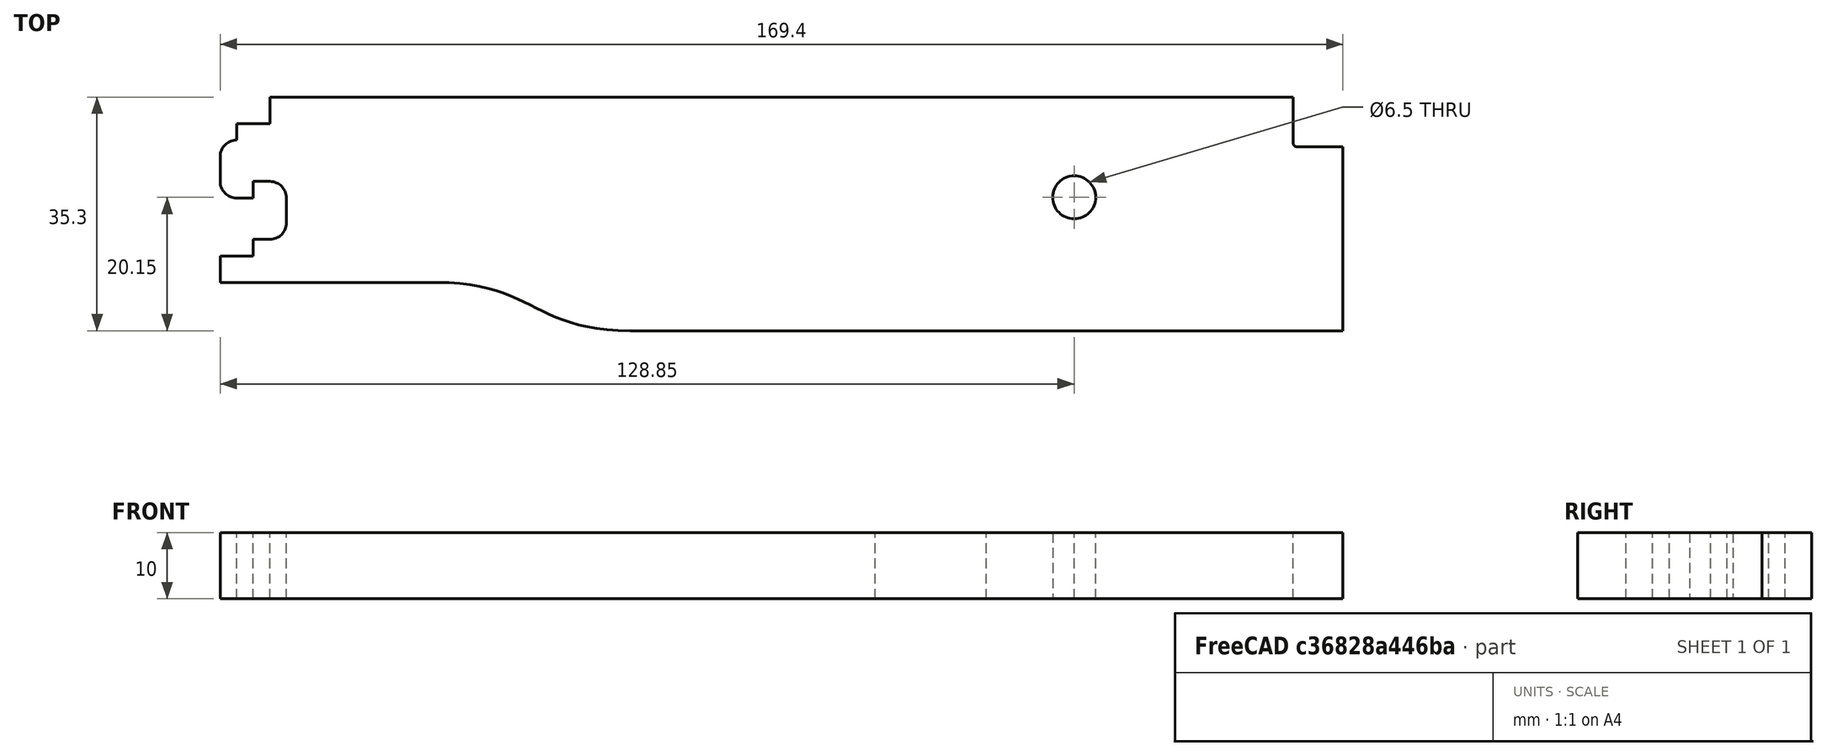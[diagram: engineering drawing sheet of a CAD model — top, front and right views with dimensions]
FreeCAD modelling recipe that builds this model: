
FCSTD DOCUMENT  (FreeCAD 0.19R0.19.2)
Label: v0_08
License: All rights reserved
LicenseURL: http://en.wikipedia.org/wiki/All_rights_reserved
objects: Sketcher::SketchObject×1, Part::Extrusion×1
note: 2 computed .brp shape members not serialized (recipe doc carries the construction recipe); baked Part::Feature solids carry a one-line shape summary decoded from their .brp

FEATURE [Sketcher::SketchObject] Sketch
  FullyConstrained = true
  sketch-geometry (43):
    g0: LineSegment StartX=0 StartY=0 StartZ=0 EndX=111.35 EndY=0 EndZ=0
    g1: Circle CenterX=111.35 CenterY=-15.15 CenterZ=0 NormalX=0 NormalY=0 NormalZ=1 AngleXU=0 Radius=3.25
    g2: LineSegment StartX=111.35 StartY=0 StartZ=0 EndX=144.4 EndY=0 EndZ=0
    g3: LineSegment StartX=144.9 StartY=-7.5 StartZ=0 EndX=151.9 EndY=-7.5 EndZ=0
    g4: LineSegment StartX=111.35 StartY=0 StartZ=0 EndX=98.1 EndY=0 EndZ=0
    g5: LineSegment StartX=111.35 StartY=0 StartZ=0 EndX=81.35 EndY=0 EndZ=0
    g6: LineSegment StartX=144.4 StartY=0 StartZ=0 EndX=144.4 EndY=-7 EndZ=0
    g7: ArcOfCircle CenterX=144.9 CenterY=-7 CenterZ=0 NormalX=0 NormalY=0 NormalZ=1 AngleXU=0 Radius=0.5 StartAngle=3.14159 EndAngle=4.71239
    g8: LineSegment StartX=151.9 StartY=-7.5 StartZ=0 EndX=151.9 EndY=-20.4 EndZ=0
    g9: LineSegment StartX=44.35 StartY=-35.3 StartZ=0 EndX=81.35 EndY=-35.3 EndZ=0
    g10: LineSegment StartX=81.35 StartY=-35.3 StartZ=0 EndX=151.9 EndY=-35.3 EndZ=0
    g11: LineSegment StartX=151.9 StartY=-20.4 StartZ=0 EndX=151.9 EndY=-35.3 EndZ=0
    g12-g16: Circle x5 (B-spline internal-alignment scaffolding for g17; pole/knot coordinates omitted)
    g17: BSplineCurve PolesCount=5 KnotsCount=3 Degree=3 IsPeriodic=0
    g18: GeomPoint X=15.15 Y=-28 Z=0
    g19: GeomPoint X=29.75 Y=-31.65 Z=0
    g20: GeomPoint X=44.35 Y=-35.3 Z=0
    g21: LineSegment StartX=15.15 StartY=-28 StartZ=0 EndX=0 EndY=-28 EndZ=0
    g22: LineSegment StartX=-10 StartY=0 StartZ=0 EndX=0 EndY=0 EndZ=0
    g23: ArcOfCircle CenterX=-15 CenterY=-9 CenterZ=0 NormalX=0 NormalY=0 NormalZ=1 AngleXU=0 Radius=2.5 StartAngle=1.5708 EndAngle=3.14159
    g24: LineSegment StartX=-17.5 StartY=-9 StartZ=0 EndX=-17.5 EndY=-11.5 EndZ=0
    g25: LineSegment StartX=-12.5 StartY=-12.75 StartZ=0 EndX=-10 EndY=-12.75 EndZ=0
    g26: LineSegment StartX=-12.5 StartY=-14 StartZ=0 EndX=-12.5 EndY=-12.75 EndZ=0
    g27: LineSegment StartX=-12.5 StartY=-21.5 StartZ=0 EndX=-10 EndY=-21.5 EndZ=0
    g28: LineSegment StartX=-12.5 StartY=-28 StartZ=0 EndX=0 EndY=-28 EndZ=0
    g29: ArcOfCircle CenterX=-10 CenterY=-15.25 CenterZ=0 NormalX=0 NormalY=0 NormalZ=1 AngleXU=0 Radius=2.5 StartAngle=0 EndAngle=1.5708
    g30: LineSegment StartX=-7.5 StartY=-15.25 StartZ=0 EndX=-7.5 EndY=-19 EndZ=0
    g31: ArcOfCircle CenterX=-10 CenterY=-19 CenterZ=0 NormalX=0 NormalY=0 NormalZ=1 AngleXU=0 Radius=2.5 StartAngle=4.71239 EndAngle=6.28319
    g32: LineSegment StartX=-12.5 StartY=-14 StartZ=0 EndX=-12.5 EndY=-15.25 EndZ=0
    g33: LineSegment StartX=-17.5 StartY=-11.5 StartZ=0 EndX=-17.5 EndY=-12.75 EndZ=0
    g34: LineSegment StartX=-15 StartY=-15.25 StartZ=0 EndX=-12.5 EndY=-15.25 EndZ=0
    g35: ArcOfCircle CenterX=-15 CenterY=-12.75 CenterZ=0 NormalX=0 NormalY=0 NormalZ=1 AngleXU=0 Radius=2.5 StartAngle=3.14159 EndAngle=4.71239
    g36: LineSegment StartX=-10 StartY=0 StartZ=0 EndX=-10 EndY=-4 EndZ=0
    g37: LineSegment StartX=-15 StartY=-4 StartZ=0 EndX=-10 EndY=-4 EndZ=0
    g38: LineSegment StartX=-15 StartY=-4 StartZ=0 EndX=-15 EndY=-6.5 EndZ=0
    g39: LineSegment StartX=-17.5 StartY=-28 StartZ=0 EndX=-12.5 EndY=-28 EndZ=0
    g40: LineSegment StartX=-17.5 StartY=-24 StartZ=0 EndX=-17.5 EndY=-28 EndZ=0
    g41: LineSegment StartX=-17.5 StartY=-24 StartZ=0 EndX=-12.5 EndY=-24 EndZ=0
    g42: LineSegment StartX=-12.5 StartY=-21.5 StartZ=0 EndX=-12.5 EndY=-24 EndZ=0
  constraints (93):
    c: Coincident(g0,g-1)
    c: PointOnObject(g0,g-1)
    c: Distance(g0) = 111.35
    c: Radius(g1) = 3.25
    c: Block(g1)
    c: Horizontal(g2)
    c: Distance(g2) = 33.05
    c: Coincident(g2,g0)
    c: Horizontal(g4)
    c: Distance(g4) = 13.25
    c: Coincident(g4,g0)
    c: Horizontal(g5)
    c: Distance(g5) = 30
    c: Coincident(g5,g0)
    c: Vertical(g6)
    c: Distance(g6) = 7
    c: Coincident(g6,g2)
    c: Coincident(g7,g6)
    c: Coincident(g7,g3)
    c: Block(g3)
    c: Block(g7)
    c: Vertical(g8)
    c: Coincident(g8,g3)
    c: Block(g8)
    c: Horizontal(g9)
    c: Distance(g9) = 37
    c: Horizontal(g10)
    c: Vertical(g11)
    c: Coincident(g10,g11)
    c: Weight(g12) = 1
    c: Equal(g12, g13-g16) x4
    c: Coincident(g17,g9)
    c: InternalAlignment(g12-g16 -> g17) x5
    c: InternalAlignment(g18,g17)
    c: InternalAlignment(g19,g17)
    c: InternalAlignment(g20,g17)
    c: Horizontal(g21)
    c: Block(g17)
    c: Block(g10)
    c: Block(g11)
    c: Block(g21)
    c: Horizontal(g22)
    c: Distance(g22) = 10
    c: Coincident(g22,g0)
    c: Vertical(g24)
    c: Block(g24)
    c: Block(g23)
    c: Distance(g25) = 2.5
    c: Horizontal(g25)
    c: Vertical(g26)
    c: Distance(g26) = 1.25
    c: Coincident(g25,g26)
    c: Horizontal(g27)
    c: Distance(g27) = 2.5
    c: Horizontal(g28)
    c: Coincident(g29,g25)
    c: Vertical(g30)
    c: Block(g29)
    c: Block(g30)
    c: Block(g31)
    c: Block(g28)
    c: Vertical(g32)
    c: Distance(g32) = 1.25
    c: Vertical(g33)
    c: Distance(g33) = 1.25
    c: Coincident(g33,g24)
    c: Horizontal(g34)
    c: Distance(g34) = 2.5
    c: Coincident(g34,g32)
    c: Coincident(g35,g34)
    c: Coincident(g35,g33)
    c: Block(g35)
    c: Vertical(g36)
    c: Distance(g36) = 4
    c: Coincident(g36,g22)
    c: Horizontal(g37)
    c: Coincident(g37,g36)
    c: Vertical(g38)
    c: Coincident(g38,g23)
    c: Coincident(g38,g37)
    c: Horizontal(g39)
    c: Distance(g39) = 5
    c: Vertical(g40)
    c: Distance(g40) = 4
    c: Coincident(g40,g39)
    c: Horizontal(g41)
    c: Block(g39)
    c: Coincident(g41,g40)
    c: Vertical(g42)
    c: Coincident(g42,g27)
    c: Coincident(g41,g42)
    c: Block(g41)
    c: Block(g27)
FEATURE [Part::Extrusion] Extrude
  Base = -> Sketch
  Dir = (0,0,1)
  DirMode = 2
  FaceMakerClass = Part::FaceMakerBullseye
  LengthFwd = 10
  LengthRev = 0
  Solid = false
  Symmetric = false
